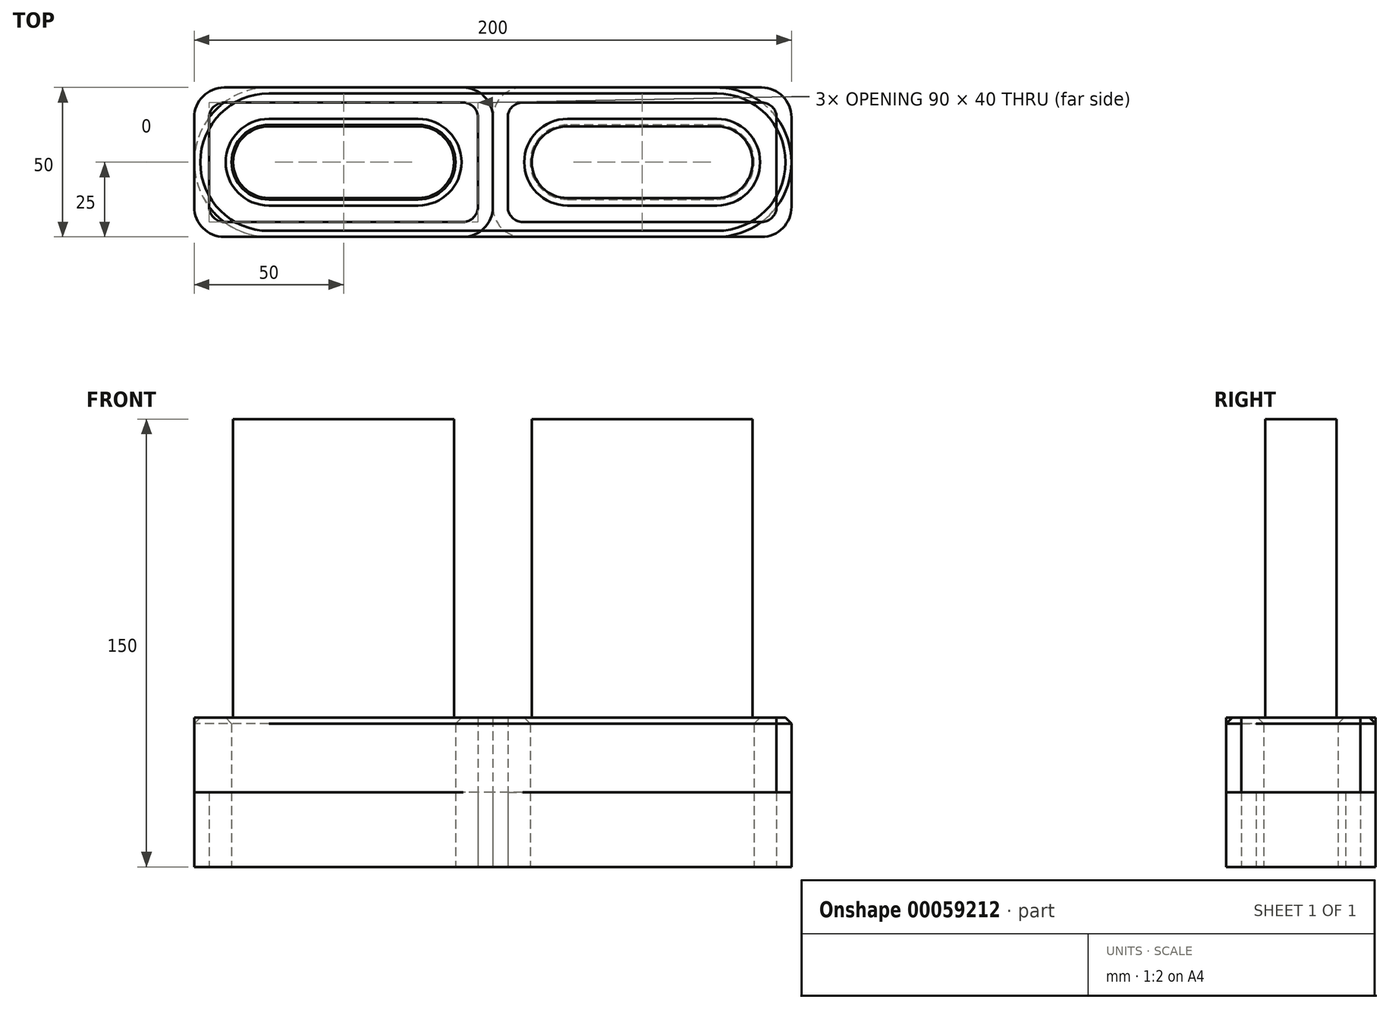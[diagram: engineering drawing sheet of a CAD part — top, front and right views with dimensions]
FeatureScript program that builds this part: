
annotation { "Feature Type Name" : "Feature", "Feature Type Description" : "" }
export const myFeature = defineFeature(function(context is Context, id is Id, definition is map)
    precondition{}
    {
        {
            var Q0;
            Q0=qCreatedBy(makeId("Top.planeOp"),FACE);
            var sketch = newSketch(context, id + "F0", { "sketchPlane" : qUnion([Q0])});
            skLineSegment(sketch, "E0.bottom", {"start": v(75, 0) * mm, "end": v(-75, 0) * mm});
            skLineSegment(sketch, "E0.top", {"start": v(75, 50) * mm, "end": v(-75, 50) * mm});
            skLineSegment(sketch, "E0.left", {"start": v(75, 0) * mm, "end": v(75, 50) * mm});
            skLineSegment(sketch, "E0.right", {"start": v(-75, 0) * mm, "end": v(-75, 50) * mm});
            skLineSegment(sketch, "E1", {"start": v(0, 0) * mm, "end": v(0, 58.91) * mm, "construction": true});
            skLineSegment(sketch, "E2.bottom", {"start": v(25, 37.5) * mm, "end": v(75, 37.5) * mm});
            skLineSegment(sketch, "E2.top", {"start": v(25, 12.5) * mm, "end": v(75, 12.5) * mm});
            skLineSegment(sketch, "E2.left", {"start": v(25, 37.5) * mm, "end": v(25, 12.5) * mm});
            skLineSegment(sketch, "E2.right", {"start": v(75, 37.5) * mm, "end": v(75, 12.5) * mm});
            skArc(sketch, "E3", {"start": v(25, 37.5) * mm, "mid": v(12.5, 25) * mm, "end": v(25, 12.5) * mm});
            skArc(sketch, "E4", {"start": v(-75, 50) * mm, "mid": v(-100, 25) * mm, "end": v(-75, 0) * mm});
            skArc(sketch, "E5", {"start": v(75, 0) * mm, "mid": v(100, 25) * mm, "end": v(75, 50) * mm});
            skArc(sketch, "E6", {"start": v(75, 12.5) * mm, "mid": v(87.5, 25) * mm, "end": v(75, 37.5) * mm});
            skLineSegment(sketch, "E7.MirrorCS", {"start": v(-75, 37.5) * mm, "end": v(-75, 12.5) * mm});
            skLineSegment(sketch, "E8.MirrorCS", {"start": v(-25, 37.5) * mm, "end": v(-25, 12.5) * mm});
            skArc(sketch, "E9.MirrorCS", {"start": v(-75, 12.5) * mm, "mid": v(-87.5, 25) * mm, "end": v(-75, 37.5) * mm});
            skArc(sketch, "E10.MirrorCS", {"start": v(-25, 37.5) * mm, "mid": v(-12.5, 25) * mm, "end": v(-25, 12.5) * mm});
            skLineSegment(sketch, "E11.MirrorCS", {"start": v(-25, 12.5) * mm, "end": v(-75, 12.5) * mm});
            skLineSegment(sketch, "E12.MirrorCS", {"start": v(-25, 37.5) * mm, "end": v(-75, 37.5) * mm});
            skSolve(sketch);
        }
        {
            var Q0;
            {var subQ0=sQuery(id+"F0.wireOp",EDGE,"E5");Q0=makeQuery(id+"F0.imprint","IMPRINT",FACE,{"disambiguationData":[TD([[makeQuery(id+"F0.imprint","IMPRINT",EDGE,{"derivedFrom":subQ0}),1.0]])]});}
            var Q1;
            {var subQ1=sQuery(id+"F0.wireOp",EDGE,"E0.bottom");Q1=makeQuery(id+"F0.imprint","IMPRINT",FACE,{"disambiguationData":[TD([[makeQuery(id+"F0.imprint","IMPRINT",EDGE,{"derivedFrom":subQ1}),-1.0]])]});}
            var Q2;
            {var subQ0=sQuery(id+"F0.wireOp",EDGE,"E4");Q2=makeQuery(id+"F0.imprint","IMPRINT",FACE,{"disambiguationData":[TD([[makeQuery(id+"F0.imprint","IMPRINT",EDGE,{"derivedFrom":subQ0}),1.0]])]});}
            extrude(context, id + "F1", {"entities" : qUnion([Q0, Q1, Q2]), "depth" : 50 * mm});
        }
        {
            var Q0;
            Q0=makeQuery(id+"F1.opExtrude","CAP_EDGE",EDGE,{"disambiguationData":[OSD([sQuery(id+"F0.wireOp",EDGE,"E0.bottom")])],"isStart":false});
            var Q1;
            Q1=makeQuery(id+"F1.opExtrude","CAP_EDGE",EDGE,{"disambiguationData":[OSD([sQuery(id+"F0.wireOp",EDGE,"E3")])],"isStart":false});
            var Q2;
            Q2=makeQuery(id+"F1.opExtrude","CAP_EDGE",EDGE,{"disambiguationData":[OSD([sQuery(id+"F0.wireOp",EDGE,"E11.MirrorCS")])],"isStart":false});
            chamfer(context, id + "F2", {"entities" : qUnion([Q0, Q1, Q2]), "width" : 2 * mm, "tangentPropagation" : true});
        }
        {
            var Q0;
            Q0=qCreatedBy(makeId("Top.planeOp"),FACE);
            var sketch = newSketch(context, id + "F3", { "sketchPlane" : qUnion([Q0])});
            skLineSegment(sketch, "E13.0", {"start": v(-25, 37.5) * mm, "end": v(-75, 37.5) * mm});
            skArc(sketch, "E13.1", {"start": v(-75, 37.5) * mm, "mid": v(-87.5, 25) * mm, "end": v(-75, 12.5) * mm});
            skLineSegment(sketch, "E13.2", {"start": v(-75, 12.5) * mm, "end": v(-25, 12.5) * mm});
            skArc(sketch, "E13.3", {"start": v(-25, 12.5) * mm, "mid": v(-12.5, 25) * mm, "end": v(-25, 37.5) * mm});
            skLineSegment(sketch, "E13.4", {"start": v(75, 37.5) * mm, "end": v(25, 37.5) * mm});
            skArc(sketch, "E13.5", {"start": v(25, 37.5) * mm, "mid": v(12.5, 25) * mm, "end": v(25, 12.5) * mm});
            skArc(sketch, "E13.6", {"start": v(75, 12.5) * mm, "mid": v(87.5, 25) * mm, "end": v(75, 37.5) * mm});
            skLineSegment(sketch, "E13.7", {"start": v(25, 12.5) * mm, "end": v(75, 12.5) * mm});
            skLineSegment(sketch, "E14.0", {"start": v(-25, 37) * mm, "end": v(-75, 37) * mm});
            skArc(sketch, "E14.1", {"start": v(-25, 13) * mm, "mid": v(-13, 25) * mm, "end": v(-25, 37) * mm});
            skLineSegment(sketch, "E14.2", {"start": v(-75, 13) * mm, "end": v(-25, 13) * mm});
            skArc(sketch, "E14.3", {"start": v(-75, 37) * mm, "mid": v(-87, 25) * mm, "end": v(-75, 13) * mm});
            skLineSegment(sketch, "E15.0", {"start": v(25, 13) * mm, "end": v(75, 13) * mm});
            skArc(sketch, "E15.1", {"start": v(25, 37) * mm, "mid": v(13, 25) * mm, "end": v(25, 13) * mm});
            skLineSegment(sketch, "E15.2", {"start": v(75, 37) * mm, "end": v(25, 37) * mm});
            skArc(sketch, "E15.3", {"start": v(75, 13) * mm, "mid": v(87, 25) * mm, "end": v(75, 37) * mm});
            skSolve(sketch);
        }
        {
            var Q0;
            Q0=makeQuery(id+"F3.imprint","IMPRINT",FACE,{"disambiguationData":[TD([[makeQuery(id+"F3.imprint","IMPRINT",EDGE,{"derivedFrom":sQuery(id+"F3.wireOp",EDGE,"E14.0")}),1.0]])]});
            var Q1;
            Q1=makeQuery(id+"F3.imprint","IMPRINT",FACE,{"disambiguationData":[TD([[makeQuery(id+"F3.imprint","IMPRINT",EDGE,{"derivedFrom":sQuery(id+"F3.wireOp",EDGE,"E15.0")}),1.0]])]});
            extrude(context, id + "F4", {"entities" : qUnion([Q0, Q1]), "depth" : 150 * mm});
        }
        {
            var Q0;
            Q0=qCreatedBy(makeId("Top.planeOp"),FACE);
            var sketch = newSketch(context, id + "F5", { "sketchPlane" : qUnion([Q0])});
            skLineSegment(sketch, "E16", {"start": v(10, 0) * mm, "end": v(90, 0) * mm});
            skLineSegment(sketch, "E17", {"start": v(100, 10) * mm, "end": v(100, 40) * mm});
            skLineSegment(sketch, "E18", {"start": v(90, 50) * mm, "end": v(10, 50) * mm});
            skLineSegment(sketch, "E19", {"start": v(0, 40) * mm, "end": v(0, 10) * mm});
            skPoint(sketch, "E20.visualSharp", {"position": v(100, 50) * mm});
            skArc(sketch, "E20.filletArc", {"start": v(100, 40) * mm, "mid": v(97.07, 47.07) * mm, "end": v(90, 50) * mm});
            skPoint(sketch, "E21.visualSharp", {"position": v(100, 0) * mm});
            skArc(sketch, "E21.filletArc", {"start": v(90, 0) * mm, "mid": v(97.07, 2.93) * mm, "end": v(100, 10) * mm});
            skPoint(sketch, "E22.visualSharp", {"position": v(0, 0) * mm});
            skArc(sketch, "E22.filletArc", {"start": v(0, 10) * mm, "mid": v(2.93, 2.93) * mm, "end": v(10, 0) * mm});
            skPoint(sketch, "E23.visualSharp", {"position": v(0, 50) * mm});
            skArc(sketch, "E23.filletArc", {"start": v(10, 50) * mm, "mid": v(2.93, 47.07) * mm, "end": v(0, 40) * mm});
            skLineSegment(sketch, "E24.MirrorCS", {"start": v(10, 100) * mm, "end": v(90, 100) * mm});
            skArc(sketch, "E25.0", {"start": v(95, 40) * mm, "mid": v(93.54, 43.54) * mm, "end": v(90, 45) * mm});
            skLineSegment(sketch, "E25.1", {"start": v(95, 10) * mm, "end": v(95, 40) * mm});
            skLineSegment(sketch, "E25.2", {"start": v(90, 45) * mm, "end": v(10, 45) * mm});
            skArc(sketch, "E25.3", {"start": v(90, 5) * mm, "mid": v(93.54, 6.46) * mm, "end": v(95, 10) * mm});
            skArc(sketch, "E25.4", {"start": v(10, 45) * mm, "mid": v(6.46, 43.54) * mm, "end": v(5, 40) * mm});
            skLineSegment(sketch, "E25.5", {"start": v(5, 40) * mm, "end": v(5, 10) * mm});
            skArc(sketch, "E25.6", {"start": v(5, 10) * mm, "mid": v(6.46, 6.46) * mm, "end": v(10, 5) * mm});
            skLineSegment(sketch, "E25.7", {"start": v(10, 5) * mm, "end": v(90, 5) * mm});
            skArc(sketch, "E26.MirrorCS", {"start": v(-95, 40) * mm, "mid": v(-93.54, 43.54) * mm, "end": v(-90, 45) * mm});
            skArc(sketch, "E27.MirrorCS", {"start": v(-90, 5) * mm, "mid": v(-93.54, 6.46) * mm, "end": v(-95, 10) * mm});
            skLineSegment(sketch, "E28.MirrorCS", {"start": v(-95, 10) * mm, "end": v(-95, 40) * mm});
            skLineSegment(sketch, "E29.MirrorCS", {"start": v(-90, 45) * mm, "end": v(-10, 45) * mm});
            skPoint(sketch, "E30.MirrorP", {"position": v(-100, 50) * mm});
            skPoint(sketch, "E31.MirrorP", {"position": v(-100, 0) * mm});
            skLineSegment(sketch, "E32.MirrorCS", {"start": v(-10, 5) * mm, "end": v(-90, 5) * mm});
            skArc(sketch, "E33.MirrorCS", {"start": v(-10, 45) * mm, "mid": v(-6.46, 43.54) * mm, "end": v(-5, 40) * mm});
            skLineSegment(sketch, "E34.MirrorCS", {"start": v(-90, 50) * mm, "end": v(-10, 50) * mm});
            skArc(sketch, "E35.MirrorCS", {"start": v(-90, 0) * mm, "mid": v(-97.07, 2.93) * mm, "end": v(-100, 10) * mm});
            skArc(sketch, "E36.MirrorCS", {"start": v(-100, 40) * mm, "mid": v(-97.07, 47.07) * mm, "end": v(-90, 50) * mm});
            skArc(sketch, "E37.MirrorCS", {"start": v(0, 10) * mm, "mid": v(-2.93, 2.93) * mm, "end": v(-10, 0) * mm});
            skArc(sketch, "E38.MirrorCS", {"start": v(-5, 10) * mm, "mid": v(-6.46, 6.46) * mm, "end": v(-10, 5) * mm});
            skLineSegment(sketch, "E39.MirrorCS", {"start": v(-10, 0) * mm, "end": v(-90, 0) * mm});
            skLineSegment(sketch, "E40.MirrorCS", {"start": v(-100, 10) * mm, "end": v(-100, 40) * mm});
            skLineSegment(sketch, "E41.MirrorCS", {"start": v(-5, 40) * mm, "end": v(-5, 10) * mm});
            skArc(sketch, "E42.MirrorCS", {"start": v(-10, 50) * mm, "mid": v(-2.93, 47.07) * mm, "end": v(0, 40) * mm});
            skSolve(sketch);
        }
        {
            var Q0;
            Q0=makeQuery(id+"F5.imprint","IMPRINT",FACE,{"disambiguationData":[TD([[makeQuery(id+"F5.imprint","IMPRINT",EDGE,{"derivedFrom":sQuery(id+"F5.wireOp",EDGE,"E16")}),1.0]])]});
            var Q1;
            Q1=makeQuery(id+"F5.imprint","IMPRINT",FACE,{"disambiguationData":[TD([[makeQuery(id+"F5.imprint","IMPRINT",EDGE,{"derivedFrom":sQuery(id+"F5.wireOp",EDGE,"E19")}),-1.0]])]});
            extrude(context, id + "F6", {"entities" : qUnion([Q0, Q1]), "depth" : 25 * mm});
        }
        {
            var Q0;
            Q0=makeQuery(id+"F5.imprint","IMPRINT",FACE,{"disambiguationData":[TD([[makeQuery(id+"F5.imprint","IMPRINT",EDGE,{"derivedFrom":sQuery(id+"F5.wireOp",EDGE,"E25.0")}),1.0]])]});
            var Q1;
            Q1=makeQuery(id+"F5.imprint","IMPRINT",FACE,{"disambiguationData":[TD([[makeQuery(id+"F5.imprint","IMPRINT",EDGE,{"derivedFrom":sQuery(id+"F5.wireOp",EDGE,"E26.MirrorCS")}),-1.0]])]});
            extrude(context, id + "F7", {"entities" : qUnion([Q0, Q1]), "depth" : 50 * mm});
        }
    });
